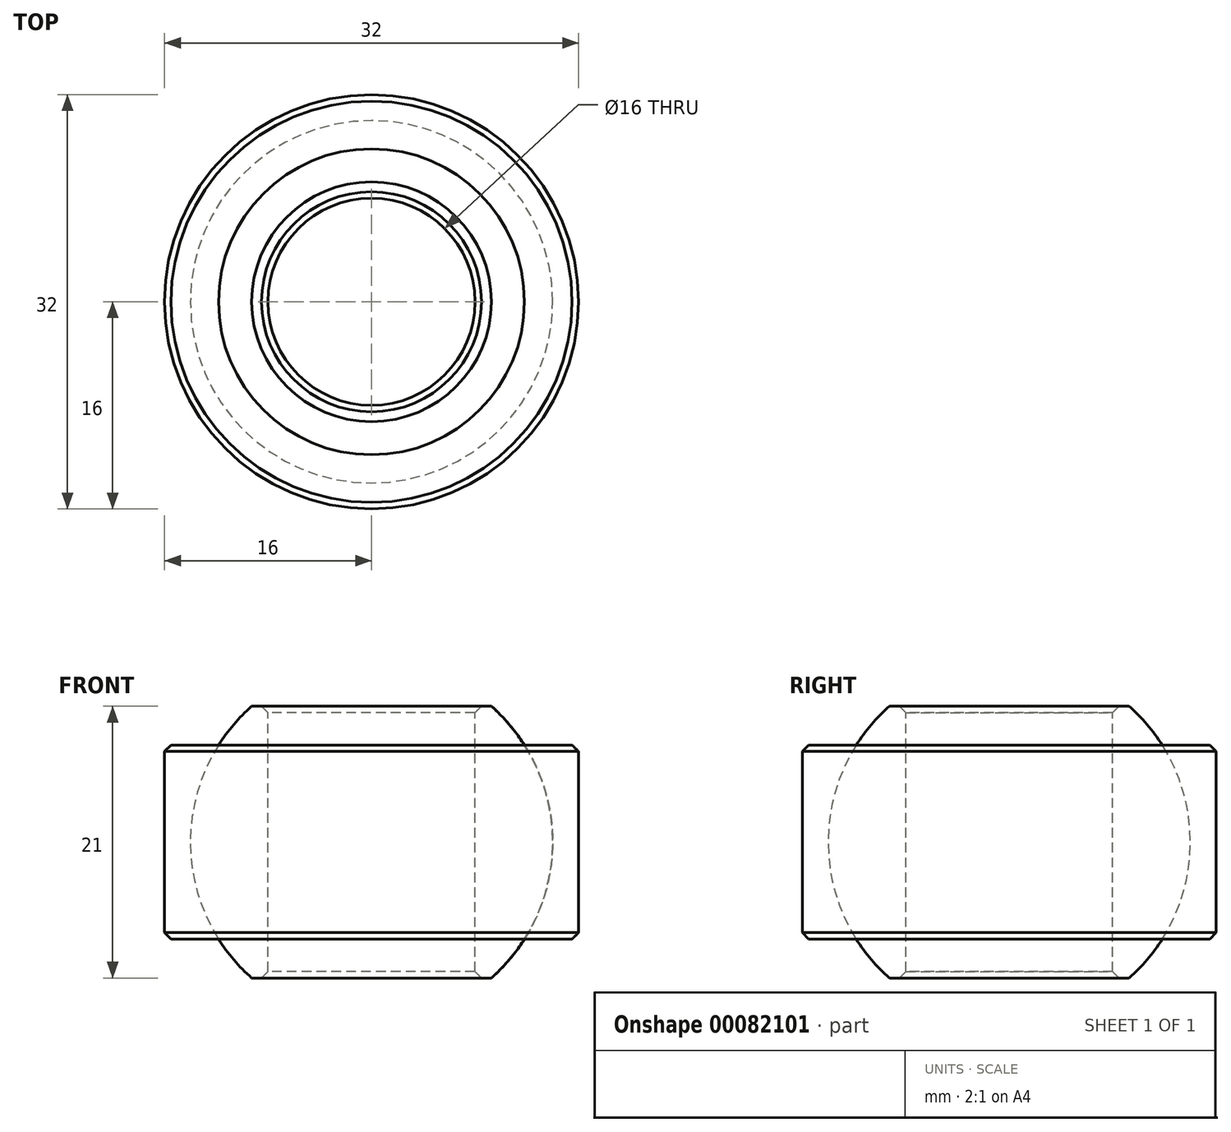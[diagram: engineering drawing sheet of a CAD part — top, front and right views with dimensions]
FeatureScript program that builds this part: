
annotation { "Feature Type Name" : "Feature", "Feature Type Description" : "" }
export const myFeature = defineFeature(function(context is Context, id is Id, definition is map)
    precondition{}
    {
        {
            var Q0;
            Q0=qCreatedBy(makeId("Top.planeOp"),FACE);
            var sketch = newSketch(context, id + "F0", { "sketchPlane" : qUnion([Q0])});
            skCircle(sketch, "E0", {"center": v(0, 0) * mm, "radius": 16 * mm});
            skSolve(sketch);
        }
        {
            var Q0;
            Q0 = qSketchRegion(id + "F0", true);
            extrude(context, id + "F1", {"entities" : qUnion([Q0]), "depth" : 15 * mm, "symmetric" : true});
        }
        {
            var Q0;
            Q0=qCreatedBy(makeId("Front.planeOp"),FACE);
            var sketch = newSketch(context, id + "F2", { "sketchPlane" : qUnion([Q0])});
            skCircle(sketch, "E1", {"center": v(0, 0) * mm, "radius": 14 * mm});
            skLineSegment(sketch, "E2", {"start": v(0, -25.5) * mm, "end": v(0, 24.66) * mm});
            skSolve(sketch);
        }
        {
            var Q0;
            {var subQ0=sQuery(id+"F2.wireOp",EDGE,"E2");var subQ1=sQuery(id+"F2.wireOp",EDGE,"E1");var subQ2=makeQuery(id+"F2.imprint","INTERSECT",VERTEX,{"disambiguationData":[OD(0.0)],"derivedFrom":[subQ1,subQ0]});Q0=makeQuery(id+"F2.imprint","IMPRINT",FACE,{"disambiguationData":[TD([[makeQuery(id+"F2.imprint","IMPRINT",EDGE,{"disambiguationData":[TD([[subQ2,-1.0]])],"derivedFrom":subQ1}),1.0]])]});}
            var Q1;
            Q1=sQuery(id+"F2.wireOp",EDGE,"E2");
            revolve(context, id + "F3", {"operationType" : NewBodyOperationType.REMOVE, "entities" : qUnion([Q0]), "axis" : qUnion([Q1]), "revolveType" : RevolveType.FULL, "oppositeDirection" : true});
        }
        {
            var Q0;
            {var subQ0=sQuery(id+"F2.wireOp",EDGE,"E2");var subQ1=sQuery(id+"F2.wireOp",EDGE,"E1");var subQ2=makeQuery(id+"F2.imprint","INTERSECT",VERTEX,{"disambiguationData":[OD(0.0)],"derivedFrom":[subQ1,subQ0]});Q0=makeQuery(id+"F2.imprint","IMPRINT",FACE,{"disambiguationData":[TD([[makeQuery(id+"F2.imprint","IMPRINT",EDGE,{"disambiguationData":[TD([[subQ2,-1.0]])],"derivedFrom":subQ1}),1.0]])]});}
            var Q1;
            Q1=sQuery(id+"F2.wireOp",EDGE,"E2");
            revolve(context, id + "F4", {"entities" : qUnion([Q0]), "axis" : qUnion([Q1]), "revolveType" : RevolveType.FULL});
        }
        {
            var Q0;
            Q0=qCreatedBy(makeId("Front.planeOp"),FACE);
            var sketch = newSketch(context, id + "F5", { "sketchPlane" : qUnion([Q0])});
            skLineSegment(sketch, "E3.bottom", {"start": v(22.57, 10.5) * mm, "end": v(-22.57, 10.5) * mm});
            skLineSegment(sketch, "E3.top", {"start": v(22.57, 31) * mm, "end": v(-22.57, 31) * mm});
            skLineSegment(sketch, "E3.left", {"start": v(22.57, 10.5) * mm, "end": v(22.57, 31) * mm});
            skLineSegment(sketch, "E3.right", {"start": v(-22.57, 10.5) * mm, "end": v(-22.57, 31) * mm});
            skPoint(sketch, "E3.middle", {"position": v(0, 20.75) * mm});
            skLineSegment(sketch, "E4.bottom", {"start": v(20.02, -21.99) * mm, "end": v(-20.02, -21.99) * mm});
            skLineSegment(sketch, "E4.top", {"start": v(20.02, -10.5) * mm, "end": v(-20.02, -10.5) * mm});
            skLineSegment(sketch, "E4.left", {"start": v(20.02, -21.99) * mm, "end": v(20.02, -10.5) * mm});
            skLineSegment(sketch, "E4.right", {"start": v(-20.02, -21.99) * mm, "end": v(-20.02, -10.5) * mm});
            skPoint(sketch, "E4.middle", {"position": v(0, -16.24) * mm});
            skSolve(sketch);
        }
        {
            var Q0;
            Q0 = qSketchRegion(id + "F5", true);
            extrude(context, id + "F6", {"entities" : qUnion([Q0]), "operationType" : NewBodyOperationType.REMOVE, "endBound" : BoundingType.THROUGH_ALL, "oppositeDirection" : true, "depth" : 25 * mm, "hasSecondDirection" : true, "secondDirectionBound" : BoundingType.THROUGH_ALL, "secondDirectionOppositeDirection" : false, "secondDirectionDepth" : 25 * mm});
        }
        {
            var Q0;
            Q0=makeQuery(id+"F6.boolean.opBoolean","COPY",FACE,{"derivedFrom":makeQuery(id+"F6.opExtrude","SWEPT_FACE",FACE,{"disambiguationData":[OSD([sQuery(id+"F5.wireOp",EDGE,"E3.bottom")])]})});
            var sketch = newSketch(context, id + "F7", { "sketchPlane" : qUnion([Q0])});
            skCircle(sketch, "E5", {"center": v(0, 0) * mm, "radius": 8 * mm});
            skSolve(sketch);
        }
        {
            var Q0;
            Q0=makeQuery(id+"F7.imprint","IMPRINT",FACE,{"disambiguationData":[TD([[makeQuery(id+"F7.imprint","IMPRINT",EDGE,{"derivedFrom":sQuery(id+"F7.wireOp",EDGE,"E5")}),1.0]])]});
            extrude(context, id + "F8", {"entities" : qUnion([Q0]), "operationType" : NewBodyOperationType.REMOVE, "endBound" : BoundingType.THROUGH_ALL, "oppositeDirection" : true, "depth" : 25 * mm});
        }
        {
            var Q0;
            Q0=makeQuery(id+"F8.boolean.opBoolean","COPY",FACE,{"derivedFrom":makeQuery(id+"F8.opExtrude","SWEPT_FACE",FACE,{"disambiguationData":[OSD([sQuery(id+"F7.wireOp",EDGE,"E5")])]})});
            var Q1;
            Q1=makeQuery(id+"F1.opExtrude","SWEPT_FACE",FACE,{"disambiguationData":[OSD([sQuery(id+"F0.wireOp",EDGE,"E0")])]});
            chamfer(context, id + "F9", {"entities" : qUnion([Q0, Q1]), "width" : 0.5 * mm, "tangentPropagation" : true});
        }
    });
